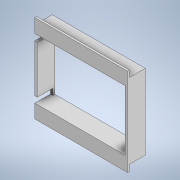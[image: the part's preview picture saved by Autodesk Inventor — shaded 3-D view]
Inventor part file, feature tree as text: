
AUTODESK INVENTOR PART (.ipt)
format: ipt  version: 2020.2 (Build 242310000, 310)  size: 175,104 bytes
history: native  units: mm
features: extrude x5, sketch x5
ambient origin geometry x8: Origin, YZ Plane, XZ Plane, XY Plane, X Axis, Y Axis, Z Axis, Center Point
bodies: Solide1 (feature_tree)
feature tree (10):
  extrude  "Extrusion1"  Depth=48.0mm
  extrude  "Extrusion3"  Depth=48.0mm
  extrude  "Extrusion4"  Depth=70.0mm
  extrude  "Extrusion5"  Depth=70.0mm
  extrude  "Extrusion6"  Depth=60.0mm
  sketch  "Esquisse1"
  sketch  "Esquisse3"
  sketch  "Esquisse4"
  sketch  "Esquisse5"
  sketch  "Esquisse6"
